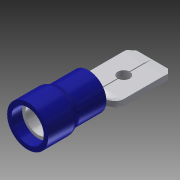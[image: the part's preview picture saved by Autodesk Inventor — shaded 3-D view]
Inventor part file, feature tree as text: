
AUTODESK INVENTOR PART (.ipt)
format: ipt  version: 2014 (Build 180170000, 170)  size: 367,616 bytes
history: native  units: in
note: dims shown in document units (in); Inventor stores cm internally (conversion verified against a paired STEP export)
features: sketch x8, extrude x6, projected_geometry x6, chamfer x4, fillet x2, shell x1, revolve x1, plane x1, loft x1, other x1
ambient origin geometry x8: Origin, YZ Plane, XZ Plane, XY Plane, X Axis, Y Axis, Z Axis, Center Point
bodies: Solid1 (feature_tree), Solid2 (feature_tree)
feature tree (31):
  extrude  "Extrusion1"  Depth=0.365in TaperAngle=0.0deg
  extrude  "Extrusion2"  Depth=0.1695in TaperAngle=0.0deg
  fillet  "Fillet1"  Radius=0.05in
  shell  "Shell1"  Thickness=0.026in
  revolve  "Revolution1"  [1 undecoded]
  plane  "Work Plane1"
  extrude  "Extrusion3"  Depth=0.02in
  loft  "Loft1"
  fillet  "Fillet3"  Radius=0.036in
  chamfer  "Chamfer1"  Angle=90.0deg  [1 undecoded]
  extrude  "Extrusion4"  Depth=0.005in TaperAngle=45.0deg
  chamfer  "Chamfer2"  Distance=0.005in Angle=45.0deg
  chamfer  "Chamfer3"  Distance=0.03in Angle=45.0deg
  chamfer  "Chamfer4"  Distance=1.0in
  extrude  "Extrusion5"  Depth=0.005in
  extrude  "Extrusion6"  Depth=0.005in TaperAngle=0.0deg
  sketch  "Sketch1"  dims[d0=0.2145in d1=0.365in d2=0.0in]
  sketch  "Sketch2"  dims[d3=0.2455in d4=0.1695in d5=0.0in d6=0.05in d7=0.026in]
  projected_geometry  "Projected Loop1"
  sketch  "Sketch3"  dims[d11=90.0deg d12=-0.06in]
  sketch  "Sketch4"  dims[d17=0.036in d18=0.0in d24=0.02in]
  sketch  "Sketch5"  dims[d27=0.003in d28=0.125in d29=45.0deg d30=0.005in d31=0.036in d32=0.0in]
  projected_geometry  "Projected Loop2"
  sketch  "Sketch6"  dims[d33=0.248in d36=0.0in d37=90.0deg]
  other  "Edges2"
  sketch  "Sketch7"  dims[d38=0.3937in d39=90.0deg d40=0.05in d41=0.005in d42=45.0deg d43=0.005in d44=0.05in d45=45.0deg d46=0.03in d47=0.05in d48=45.0deg]
  projected_geometry  "Projected Loop3"
  sketch  "Sketch8"  dims[d49=0.0715in d50=1.0in d51=0.0in d52=0.005in d53=0.005in d54=0.0in d55=0.0135in d56=0.2925in d57=0.09in]
  projected_geometry  "Projected Loop4"
  projected_geometry  "Project Cut Edges1"
  projected_geometry  "Project Cut Edges2"
note: 2 required parameter values undecoded (feature->parameter linkage not recoverable at this tier; creation-order binding heuristic only, values carry confidence <= 0.55)